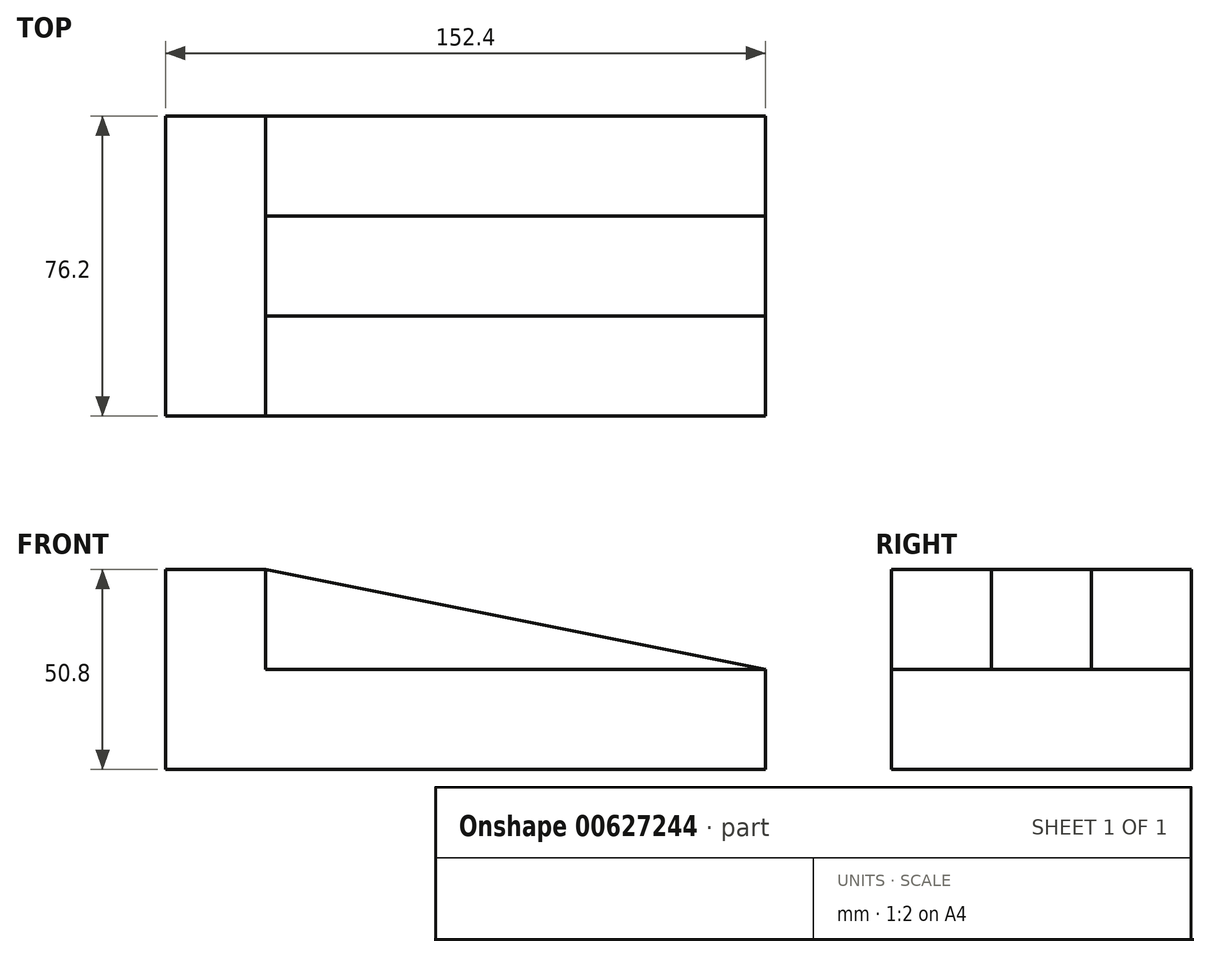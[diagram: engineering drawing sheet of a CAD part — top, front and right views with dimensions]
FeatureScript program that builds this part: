
annotation { "Feature Type Name" : "Feature", "Feature Type Description" : "" }
export const myFeature = defineFeature(function(context is Context, id is Id, definition is map)
    precondition{}
    {
        {
            var Q0;
            Q0=qCreatedBy(makeId("Front.planeOp"),FACE);
            var sketch = newSketch(context, id + "F0", { "sketchPlane" : qUnion([Q0])});
            skLineSegment(sketch, "E0.bottom", {"start": v(0, 0) * mm, "end": v(152.4, 0) * mm});
            skLineSegment(sketch, "E0.top", {"start": v(0, 50.8) * mm, "end": v(152.4, 50.8) * mm});
            skLineSegment(sketch, "E0.left", {"start": v(0, 0) * mm, "end": v(0, 50.8) * mm});
            skLineSegment(sketch, "E0.right", {"start": v(152.4, 0) * mm, "end": v(152.4, 50.8) * mm});
            skLineSegment(sketch, "E1.bottom", {"start": v(25.4, 50.8) * mm, "end": v(152.4, 50.8) * mm});
            skLineSegment(sketch, "E1.top", {"start": v(25.4, 25.4) * mm, "end": v(152.4, 25.4) * mm});
            skLineSegment(sketch, "E1.left", {"start": v(25.4, 50.8) * mm, "end": v(25.4, 25.4) * mm});
            skLineSegment(sketch, "E1.right", {"start": v(152.4, 50.8) * mm, "end": v(152.4, 25.4) * mm});
            skLineSegment(sketch, "E2", {"start": v(25.4, 50.8) * mm, "end": v(152.4, 25.4) * mm});
            skSolve(sketch);
        }
        {
            var Q0;
            Q0=makeQuery(id+"F0.imprint","IMPRINT",FACE,{"disambiguationData":[TD([[makeQuery(id+"F0.imprint","IMPRINT",EDGE,{"derivedFrom":sQuery(id+"F0.wireOp",EDGE,"E0.bottom")}),1.0]])]});
            extrude(context, id + "F1", {"entities" : qUnion([Q0]), "depth" : 25.4 * mm, "offsetDistance" : 25.4 * mm});
        }
        {
            var Q0;
            Q0=makeQuery(id+"F1.opExtrude","CAP_FACE",FACE,{"disambiguationData":[OSD([sQuery(id+"F0.wireOp",EDGE,"E0.bottom"),sQuery(id+"F0.wireOp",EDGE,"E0.top"),sQuery(id+"F0.wireOp",EDGE,"E0.left"),sQuery(id+"F0.wireOp",EDGE,"E0.right"),sQuery(id+"F0.wireOp",EDGE,"E1.top"),sQuery(id+"F0.wireOp",EDGE,"E1.left")])],"isStart":false});
            extrude(context, id + "F2", {"entities" : qUnion([Q0]), "operationType" : NewBodyOperationType.ADD, "depth" : 50.8 * mm, "offsetDistance" : 25.4 * mm});
        }
        {
            var Q0;
            {var subQ0=sQuery(id+"F0.wireOp",EDGE,"E0.left");Q0=makeQuery(id+"F2.boolean.opBoolean","MERGE",FACE,{"derivedFrom":[makeQuery(id+"F1.opExtrude","SWEPT_FACE",FACE,{"disambiguationData":[OSD([subQ0])]}),makeQuery(id+"F2.opExtrude","SWEPT_FACE",FACE,{"disambiguationData":[OSD([subQ0])]})]});}
            var sketch = newSketch(context, id + "F3", { "sketchPlane" : qUnion([Q0])});
            skLineSegment(sketch, "E3", {"start": v(0, 0) * mm, "end": v(0, 25.4) * mm});
            skLineSegment(sketch, "E4", {"start": v(0, 25.4) * mm, "end": v(76.2, 25.4) * mm});
            skLineSegment(sketch, "E5", {"start": v(0, 25.4) * mm, "end": v(25.4, 25.4) * mm});
            skLineSegment(sketch, "E6", {"start": v(25.4, 25.4) * mm, "end": v(25.4, 50.8) * mm});
            skLineSegment(sketch, "E7", {"start": v(25.4, 50.8) * mm, "end": v(50.8, 50.8) * mm});
            skLineSegment(sketch, "E8", {"start": v(50.8, 50.8) * mm, "end": v(50.8, 25.4) * mm});
            skLineSegment(sketch, "E9", {"start": v(25.4, 25.4) * mm, "end": v(50.8, 25.4) * mm});
            skSolve(sketch);
        }
        {
            var Q0;
            Q0 = qSketchRegion(id + "F3", true);
            extrude(context, id + "F4", {"entities" : qUnion([Q0]), "operationType" : NewBodyOperationType.ADD, "oppositeDirection" : true, "depth" : 152.4 * mm, "offsetDistance" : 25.4 * mm});
        }
        {
            var Q0;
            Q0=makeQuery(id+"F4.opExtrude","SWEPT_FACE",FACE,{"disambiguationData":[OSD([sQuery(id+"F3.wireOp",EDGE,"E8")])]});
            var sketch = newSketch(context, id + "F5", { "sketchPlane" : qUnion([Q0])});
            skLineSegment(sketch, "E10", {"start": v(25.4, 50.8) * mm, "end": v(152.4, 25.4) * mm});
            skLineSegment(sketch, "E11", {"start": v(152.4, 25.4) * mm, "end": v(152.4, 50.8) * mm});
            skLineSegment(sketch, "E12", {"start": v(152.4, 50.8) * mm, "end": v(25.4, 50.8) * mm});
            skSolve(sketch);
        }
        {
            var Q0;
            Q0 = qSketchRegion(id + "F5", true);
            extrude(context, id + "F6", {"entities" : qUnion([Q0]), "operationType" : NewBodyOperationType.REMOVE, "oppositeDirection" : true, "depth" : 25.4 * mm, "offsetDistance" : 25.4 * mm});
        }
    });
